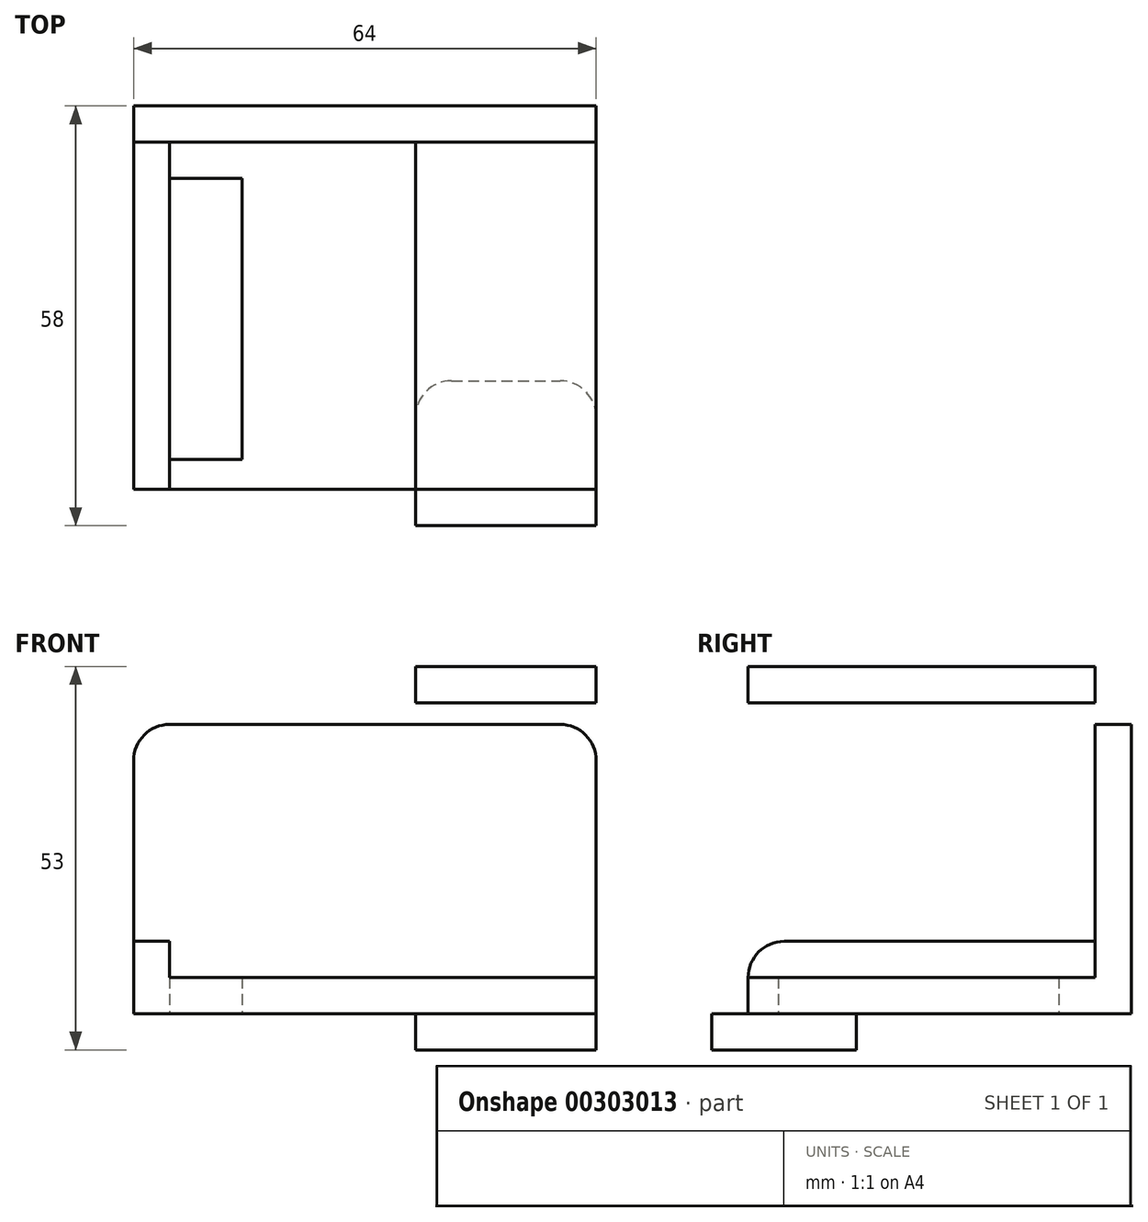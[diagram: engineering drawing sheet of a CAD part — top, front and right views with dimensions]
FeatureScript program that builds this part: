
annotation { "Feature Type Name" : "Feature", "Feature Type Description" : "" }
export const myFeature = defineFeature(function(context is Context, id is Id, definition is map)
    precondition{}
    {
        {
            var Q0;
            Q0=qCreatedBy(makeId("Top.planeOp"),FACE);
            var sketch = newSketch(context, id + "F0", { "sketchPlane" : qUnion([Q0])});
            skLineSegment(sketch, "E0.bottom", {"start": v(24.5, 21.5) * mm, "end": v(-24.5, 21.5) * mm});
            skLineSegment(sketch, "E0.top", {"start": v(24.5, -21.5) * mm, "end": v(-24.5, -21.5) * mm});
            skLineSegment(sketch, "E0.left", {"start": v(24.5, 21.5) * mm, "end": v(24.5, -21.5) * mm});
            skLineSegment(sketch, "E0.right", {"start": v(-24.5, 21.5) * mm, "end": v(-24.5, -21.5) * mm});
            skPoint(sketch, "E0.middle", {"position": v(0, 0) * mm});
            skLineSegment(sketch, "E1.bottom", {"start": v(-24.5, 21.5) * mm, "end": v(-34.5, 21.5) * mm});
            skLineSegment(sketch, "E1.top", {"start": v(-24.5, -21.5) * mm, "end": v(-34.5, -21.5) * mm});
            skLineSegment(sketch, "E1.right", {"start": v(-34.5, 21.5) * mm, "end": v(-34.5, -21.5) * mm});
            skLineSegment(sketch, "E2.bottom", {"start": v(-34.5, 21.5) * mm, "end": v(-39.5, 21.5) * mm});
            skLineSegment(sketch, "E2.top", {"start": v(-34.5, -21.5) * mm, "end": v(-39.5, -21.5) * mm});
            skLineSegment(sketch, "E2.right", {"start": v(-39.5, 21.5) * mm, "end": v(-39.5, -21.5) * mm});
            skLineSegment(sketch, "E3.bottom", {"start": v(-39.5, 21.5) * mm, "end": v(24.5, 21.5) * mm});
            skLineSegment(sketch, "E3.top", {"start": v(-39.5, 26.5) * mm, "end": v(24.5, 26.5) * mm});
            skLineSegment(sketch, "E3.left", {"start": v(-39.5, 21.5) * mm, "end": v(-39.5, 26.5) * mm});
            skLineSegment(sketch, "E3.right", {"start": v(24.5, 21.5) * mm, "end": v(24.5, 26.5) * mm});
            skLineSegment(sketch, "E4.top", {"start": v(-39.5, 31.5) * mm, "end": v(24.5, 31.5) * mm});
            skLineSegment(sketch, "E4.left", {"start": v(-39.5, 26.5) * mm, "end": v(-39.5, 31.5) * mm});
            skLineSegment(sketch, "E4.right", {"start": v(24.5, 26.5) * mm, "end": v(24.5, 31.5) * mm});
            skLineSegment(sketch, "E5", {"start": v(-34.5, 21.5) * mm, "end": v(-34.5, 26.5) * mm});
            skLineSegment(sketch, "E6", {"start": v(-34.5, -17.35) * mm, "end": v(-24.5, -17.35) * mm});
            skSolve(sketch);
        }
        {
            var Q0;
            {var subQ1=sQuery(id+"F0.wireOp",EDGE,"E0.top");Q0=makeQuery(id+"F0.imprint","IMPRINT",FACE,{"disambiguationData":[TD([[makeQuery(id+"F0.imprint","IMPRINT",EDGE,{"derivedFrom":subQ1}),-1.0]])]});}
            var Q1;
            {var subQ0=sQuery(id+"F0.wireOp",EDGE,"E1.top");Q1=makeQuery(id+"F0.imprint","IMPRINT",FACE,{"disambiguationData":[TD([[makeQuery(id+"F0.imprint","IMPRINT",EDGE,{"derivedFrom":subQ0}),-1.0]])]});}
            var Q2;
            {var subQ0=sQuery(id+"F0.wireOp",EDGE,"E3.right");Q2=makeQuery(id+"F0.imprint","IMPRINT",FACE,{"disambiguationData":[TD([[makeQuery(id+"F0.imprint","IMPRINT",EDGE,{"derivedFrom":subQ0}),1.0]])]});}
            extrude(context, id + "F1", {"entities" : qUnion([Q0, Q1, Q2]), "depth" : 5 * mm});
        }
        {
            var Q0;
            {var subQ2=sQuery(id+"F0.wireOp",EDGE,"E2.top");Q0=makeQuery(id+"F0.imprint","IMPRINT",FACE,{"disambiguationData":[TD([[makeQuery(id+"F0.imprint","IMPRINT",EDGE,{"derivedFrom":subQ2}),-1.0]])]});}
            var Q1;
            {var subQ2=sQuery(id+"F0.wireOp",EDGE,"E3.left");Q1=makeQuery(id+"F0.imprint","IMPRINT",FACE,{"disambiguationData":[TD([[makeQuery(id+"F0.imprint","IMPRINT",EDGE,{"derivedFrom":subQ2}),-1.0]])]});}
            extrude(context, id + "F2", {"entities" : qUnion([Q0, Q1]), "operationType" : NewBodyOperationType.ADD, "depth" : 10 * mm});
        }
        {
            var Q0;
            Q0=makeQuery(id+"F0.imprint","IMPRINT",FACE,{"disambiguationData":[TD([[makeQuery(id+"F0.imprint","IMPRINT",EDGE,{"derivedFrom":sQuery(id+"F0.wireOp",EDGE,"E4.top")}),-1.0]])]});
            extrude(context, id + "F3", {"entities" : qUnion([Q0]), "operationType" : NewBodyOperationType.ADD, "depth" : 40 * mm});
        }
        {
            var Q0;
            Q0=makeQuery(id+"F3.opExtrude","CAP_EDGE",EDGE,{"disambiguationData":[OSD([sQuery(id+"F0.wireOp",EDGE,"E4.left")])],"isStart":false});
            var Q1;
            Q1=makeQuery(id+"F3.opExtrude","CAP_EDGE",EDGE,{"disambiguationData":[OSD([sQuery(id+"F0.wireOp",EDGE,"E4.right")])],"isStart":false});
            var Q2;
            Q2=makeQuery(id+"F2.opExtrude","CAP_EDGE",EDGE,{"disambiguationData":[OSD([sQuery(id+"F0.wireOp",EDGE,"E2.top")])],"isStart":false});
            var Q3;
            Q3=makeQuery(id+"F2.opExtrude","CAP_EDGE",EDGE,{"disambiguationData":[OSD([sQuery(id+"F0.wireOp",EDGE,"E3.top")])],"isStart":false});
            fillet(context, id + "F4", {"entities" : qUnion([Q0, Q1, Q2, Q3]), "radius" : 5 * mm, "tangentPropagation" : true, "allowEdgeOverflow" : false});
        }
        {
            var Q0;
            Q0=makeQuery(id+"F3.boolean.opBoolean","MERGE",FACE,{"derivedFrom":[makeQuery(id+"F1.opExtrude","SWEPT_FACE",FACE,{"disambiguationData":[OSD([sQuery(id+"F0.wireOp",EDGE,"E0.left"),sQuery(id+"F0.wireOp",EDGE,"E3.right")])]}),makeQuery(id+"F3.opExtrude","SWEPT_FACE",FACE,{"disambiguationData":[OSD([sQuery(id+"F0.wireOp",EDGE,"E4.right")])]})]});
            var sketch = newSketch(context, id + "F5", { "sketchPlane" : qUnion([Q0])});
            skLineSegment(sketch, "E7.bottom", {"start": v(-6.5, 0) * mm, "end": v(-26.5, 0) * mm});
            skLineSegment(sketch, "E7.top", {"start": v(-6.5, -5) * mm, "end": v(-26.5, -5) * mm});
            skLineSegment(sketch, "E7.left", {"start": v(-6.5, 0) * mm, "end": v(-6.5, -5) * mm});
            skLineSegment(sketch, "E7.right", {"start": v(-26.5, 0) * mm, "end": v(-26.5, -5) * mm});
            skLineSegment(sketch, "E8.bottom", {"start": v(-21.5, 0) * mm, "end": v(-26.5, 0) * mm});
            skLineSegment(sketch, "E8.top", {"start": v(-21.5, 48) * mm, "end": v(-26.5, 48) * mm});
            skLineSegment(sketch, "E8.left", {"start": v(-21.5, 0) * mm, "end": v(-21.5, 48) * mm});
            skLineSegment(sketch, "E8.right", {"start": v(-26.5, 0) * mm, "end": v(-26.5, 48) * mm});
            skLineSegment(sketch, "E9.bottom", {"start": v(-21.5, 48) * mm, "end": v(26.5, 48) * mm});
            skLineSegment(sketch, "E9.top", {"start": v(-21.5, 43) * mm, "end": v(26.5, 43) * mm});
            skLineSegment(sketch, "E9.left", {"start": v(-21.5, 48) * mm, "end": v(-21.5, 43) * mm});
            skLineSegment(sketch, "E9.right", {"start": v(26.5, 48) * mm, "end": v(26.5, 43) * mm});
            skLineSegment(sketch, "E10.bottom", {"start": v(26.5, 43) * mm, "end": v(21.5, 43) * mm});
            skLineSegment(sketch, "E10.top", {"start": v(26.5, 22.6) * mm, "end": v(21.5, 22.6) * mm});
            skLineSegment(sketch, "E10.left", {"start": v(26.5, 43) * mm, "end": v(26.5, 22.6) * mm});
            skLineSegment(sketch, "E10.right", {"start": v(21.5, 43) * mm, "end": v(21.5, 22.6) * mm});
            skSolve(sketch);
        }
        {
            var Q0;
            Q0=makeQuery(id+"F5.imprint","IMPRINT",FACE,{"disambiguationData":[TD([[makeQuery(id+"F5.imprint","IMPRINT",EDGE,{"derivedFrom":sQuery(id+"F5.wireOp",EDGE,"E7.bottom")}),1.0]])]});
            var Q1;
            {var subQ1=sQuery(id+"F5.wireOp",EDGE,"E8.bottom");Q1=makeQuery(id+"F5.imprint","IMPRINT",FACE,{"disambiguationData":[TD([[makeQuery(id+"F5.imprint","IMPRINT",EDGE,{"derivedFrom":subQ1}),-1.0]])]});}
            var Q2;
            Q2=makeQuery(id+"F5.imprint","IMPRINT",FACE,{"disambiguationData":[TD([[makeQuery(id+"F5.imprint","IMPRINT",EDGE,{"derivedFrom":sQuery(id+"F5.wireOp",EDGE,"E9.bottom")}),-1.0]])]});
            var Q3;
            {var subQ5=sQuery(id+"F5.wireOp",EDGE,"E10.bottom");Q3=makeQuery(id+"F5.imprint","IMPRINT",FACE,{"disambiguationData":[TD([[makeQuery(id+"F5.imprint","IMPRINT",EDGE,{"derivedFrom":subQ5}),1.0]])]});}
            extrude(context, id + "F6", {"entities" : qUnion([Q0, Q1, Q2, Q3]), "oppositeDirection" : true, "depth" : 25 * mm});
        }
        {
            var Q0;
            Q0=makeQuery(id+"F6.opExtrude","CAP_EDGE",EDGE,{"disambiguationData":[OSD([sQuery(id+"F5.wireOp",EDGE,"E10.top")])],"isStart":true});
            var Q1;
            Q1=makeQuery(id+"F6.opExtrude","CAP_EDGE",EDGE,{"disambiguationData":[OSD([sQuery(id+"F5.wireOp",EDGE,"E10.top")])],"isStart":false});
            var Q2;
            Q2=makeQuery(id+"F6.opExtrude","CAP_EDGE",EDGE,{"disambiguationData":[OSD([sQuery(id+"F5.wireOp",EDGE,"E7.left")])],"isStart":true});
            var Q3;
            Q3=makeQuery(id+"F6.opExtrude","CAP_EDGE",EDGE,{"disambiguationData":[OSD([sQuery(id+"F5.wireOp",EDGE,"E7.left")])],"isStart":false});
            fillet(context, id + "F7", {"entities" : qUnion([Q0, Q1, Q2, Q3]), "radius" : 5 * mm, "tangentPropagation" : true, "allowEdgeOverflow" : false});
        }
    });
